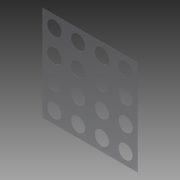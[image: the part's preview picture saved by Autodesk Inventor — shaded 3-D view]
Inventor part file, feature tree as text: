
AUTODESK INVENTOR PART (.ipt)
format: ipt  version: 2014 (Build 180170000, 170)  size: 185,856 bytes
history: native  units: in
note: dims shown in document units (in); Inventor stores cm internally (conversion verified against a paired STEP export)
features: extrude x3, sketch x3, pattern_linear x1
ambient origin geometry x8: Origin, YZ Plane, XZ Plane, XY Plane, X Axis, Y Axis, Z Axis, Center Point
bodies: Body1 (feature_tree)
feature tree (7):
  extrude  "Extrusion1"  Depth=20.0in
  extrude  "Extrusion3"  Depth=0.0312in
  pattern_linear  "Rectangular Pattern1"  Spacing1=2.5in  [1 undecoded]
  extrude  "Extrusion4"  Depth=2.5in
  sketch  "Sketch1"  dims[d5=20.0in d6=20.0in]
  sketch  "Sketch3"  dims[d10=0.0312in d11=0.0in d12=1.0in]
  sketch  "Sketch4"  dims[d26=3.0in d27=2.5in d28=2.5in d29=0.0625in d30=0.0in d31=1.5748in d33=5.0in d34=1.5748in d36=5.0in d67=0.196in d69=0.25in d70=0.25in d106=0.196in d107=0.7874in d109=0.5in d110=0.7874in d112=0.5in d115=0.25in d116=4.0in d117=0.75in d118=3.0in d119=0.196in d120=0.25in d121=0.25in d123=0.25in d124=1.0in d125=0.5in d126=0.196in d127=0.25in d128=1.0in d129=0.0in d130=2.0in d131=0.25in]
note: 1 required parameter value undecoded (feature->parameter linkage not recoverable at this tier; creation-order binding heuristic only, values carry confidence <= 0.55)
